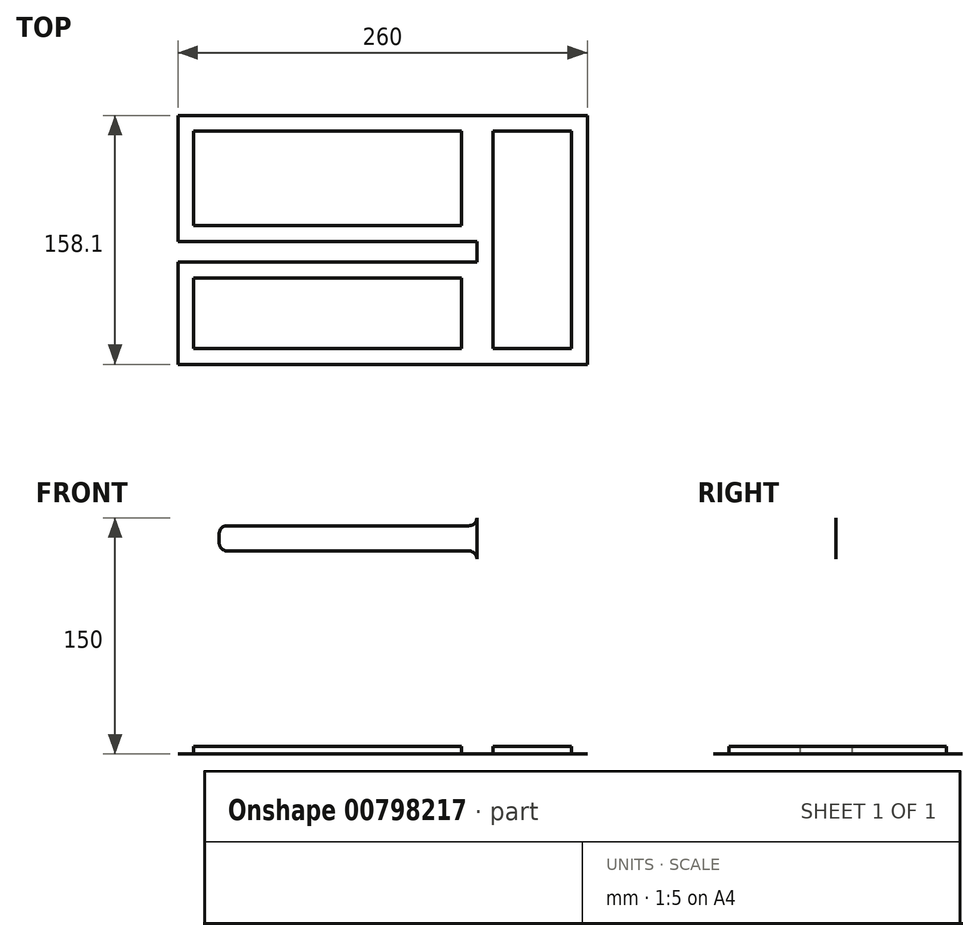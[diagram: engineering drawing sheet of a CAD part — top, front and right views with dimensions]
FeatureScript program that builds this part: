
annotation { "Feature Type Name" : "Feature", "Feature Type Description" : "" }
export const myFeature = defineFeature(function(context is Context, id is Id, definition is map)
    precondition{}
    {
        {
            var Q0;
            Q0=qCreatedBy(makeId("Front.planeOp"),FACE);
            var sketch = newSketch(context, id + "F0", { "sketchPlane" : qUnion([Q0])});
            skLineSegment(sketch, "E0.bottom", {"start": v(100, 120) * mm, "end": v(-100, 120) * mm});
            skLineSegment(sketch, "E0.top", {"start": v(100, -120) * mm, "end": v(-100, -120) * mm});
            skLineSegment(sketch, "E0.left", {"start": v(100, 120) * mm, "end": v(100, -120) * mm});
            skLineSegment(sketch, "E0.right", {"start": v(-100, 120) * mm, "end": v(-100, -120) * mm});
            skPoint(sketch, "E0.middle", {"position": v(0, 0) * mm});
            skSolve(sketch);
        }
        {
            var Q0;
            Q0=makeQuery(id+"F0.imprint","IMPRINT",FACE,{"disambiguationData":[TD([[makeQuery(id+"F0.imprint","IMPRINT",EDGE,{"derivedFrom":sQuery(id+"F0.wireOp",EDGE,"E0.bottom")}),1.0]])]});
            extrude(context, id + "F1", {"entities" : qUnion([Q0]), "depth" : 1 / 50.8 * mm, "offsetDistance" : 25 * mm});
        }
        {
            var Q0;
            Q0=makeQuery(id+"F1.opExtrude","SWEPT_FACE",FACE,{"disambiguationData":[OSD([sQuery(id+"F0.wireOp",EDGE,"E0.left")])]});
            extrude(context, id + "F2", {"entities" : qUnion([Q0]), "operationType" : NewBodyOperationType.ADD, "depth" : 120 * mm, "offsetDistance" : 25 * mm});
        }
        {
            var Q0;
            Q0=makeQuery(id+"F1.opExtrude","CAP_FACE",FACE,{"disambiguationData":[OSD([sQuery(id+"F0.wireOp",EDGE,"E0.bottom"),sQuery(id+"F0.wireOp",EDGE,"E0.top"),sQuery(id+"F0.wireOp",EDGE,"E0.left"),sQuery(id+"F0.wireOp",EDGE,"E0.right")])],"isStart":false});
            var sketch = newSketch(context, id + "F3", { "sketchPlane" : qUnion([Q0])});
            skLineSegment(sketch, "E1.bottom", {"start": v(-100, 120) * mm, "end": v(-13.6, 120) * mm});
            skLineSegment(sketch, "E1.top", {"start": v(-100, -44) * mm, "end": v(-61.8, -44) * mm});
            skLineSegment(sketch, "E1.left", {"start": v(-100, 120) * mm, "end": v(-100, -44) * mm});
            skLineSegment(sketch, "E1.right", {"start": v(-13.6, 120) * mm, "end": v(-13.6, -44) * mm});
            skPoint(sketch, "E2", {"position": v(-56.8, -44) * mm});
            skLineSegment(sketch, "E3", {"start": v(-56.8, -44) * mm, "end": v(-56.8, -58) * mm, "construction": true});
            skLineSegment(sketch, "E4", {"start": v(-61.8, -58) * mm, "end": v(-59.67, -58) * mm});
            skPoint(sketch, "E5", {"position": v(-56.8, -58) * mm});
            skLineSegment(sketch, "E6", {"start": v(-51.8, -58) * mm, "end": v(-51.8, -44) * mm});
            skLineSegment(sketch, "E7", {"start": v(-61.8, -58) * mm, "end": v(-61.8, -44) * mm});
            skLineSegment(sketch, "E8.trimOffspring", {"start": v(-51.8, -44) * mm, "end": v(-13.6, -44) * mm});
            skPoint(sketch, "E9", {"position": v(-56.8, -67.99) * mm});
            skLineSegment(sketch, "E10", {"start": v(-56.8, -58) * mm, "end": v(-56.8, -67.99) * mm, "construction": true});
            skLineSegment(sketch, "E11", {"start": v(-59, -67.98) * mm, "end": v(-59.67, -58) * mm});
            skLineSegment(sketch, "E12", {"start": v(-54.6, -68) * mm, "end": v(-54.6, -58) * mm});
            skLineSegment(sketch, "E13.trimOffspring", {"start": v(-54.6, -58) * mm, "end": v(-51.8, -58) * mm});
            skFitSpline(sketch, "E14", {"points": [v(-56.8, -67.99) * mm, v(-48.64, -88.4) * mm, v(-5.79, -87.52) * mm, v(11.38, -64.83) * mm], "startDerivative": vector(1.52, -51.58) * mm, "endDerivative": vector(22.85, 51.61) * mm, "construction": true});
            skFitSpline(sketch, "E15", {"points": [v(11.38, -64.83) * mm, v(19.18, -38.13) * mm, v(0, -6.57) * mm, v(20.17, 28.85) * mm, v(11.38, 54.12) * mm], "startDerivative": vector(47.45, 107.17) * mm, "endDerivative": vector(-56.95, 91.36) * mm, "construction": true});
            skLineSegment(sketch, "E16", {"start": v(8.93, -70.37) * mm, "end": v(11.38, -64.83) * mm, "construction": true});
            skLineSegment(sketch, "E17", {"start": v(15.02, -56.6) * mm, "end": v(11.38, -64.83) * mm, "construction": true});
            skFitSpline(sketch, "E18.0", {"points": [v(13.4, -65.72) * mm, v(13.86, -64.66) * mm, v(14.94, -62.44) * mm, v(16.76, -58.93) * mm, v(18.6, -55.26) * mm, v(20.25, -51.44) * mm, v(21.5, -47.47) * mm, v(22.03, -44.02) * mm, v(22, -41.2) * mm, v(21.77, -39.42) * mm, v(21.44, -38) * mm, v(21, -36.57) * mm, v(20.3, -34.84) * mm, v(19.24, -32.83) * mm, v(17.58, -30.22) * mm, v(15.18, -27.04) * mm, v(12.04, -23.32) * mm, v(8.92, -19.67) * mm, v(6.1, -16.08) * mm, v(4.23, -13.16) * mm, v(3.15, -10.9) * mm, v(2.57, -9.25) * mm, v(2.3, -7.92) * mm, v(2.2, -6.88) * mm, v(2.2, -5.84) * mm, v(2.35, -4.5) * mm, v(2.8, -2.82) * mm, v(3.48, -1.06) * mm, v(4.69, 1.37) * mm, v(6.69, 4.54) * mm, v(9.62, 8.45) * mm, v(12.8, 12.45) * mm, v(15.98, 16.52) * mm, v(18.4, 19.96) * mm, v(20.05, 22.76) * mm, v(21.12, 24.9) * mm, v(21.84, 26.7) * mm, v(22.28, 28.19) * mm, v(22.62, 29.67) * mm, v(22.87, 31.52) * mm, v(22.9, 34.42) * mm, v(22.35, 37.94) * mm, v(21, 41.92) * mm, v(19.21, 45.66) * mm, v(17.18, 49.15) * mm, v(15.1, 52.39) * mm, v(13.83, 54.35) * mm, v(13.25, 55.28) * mm]});
            skFitSpline(sketch, "E18.1", {"points": [v(-59, -68.05) * mm, v(-58.97, -69.18) * mm, v(-58.8, -71.97) * mm, v(-58.06, -76.25) * mm, v(-56.98, -79.86) * mm, v(-55.87, -82.58) * mm, v(-54.41, -85.25) * mm, v(-52.86, -87.35) * mm, v(-51.4, -88.91) * mm, v(-50.18, -90) * mm, v(-48.84, -91.01) * mm, v(-46.94, -92.2) * mm, v(-44.36, -93.46) * mm, v(-40.97, -94.6) * mm, v(-37.37, -95.4) * mm, v(-32.34, -96.04) * mm, v(-25.75, -96.04) * mm, v(-19.13, -95.04) * mm, v(-14.02, -93.67) * mm, v(-10.34, -92.35) * mm, v(-7.44, -91) * mm, v(-5.24, -89.78) * mm, v(-3.15, -88.46) * mm, v(-0.75, -86.66) * mm, v(2.68, -83.51) * mm, v(6.2, -79.27) * mm, v(9.42, -74.12) * mm, v(11.79, -69.38) * mm, v(12.92, -66.79) * mm, v(13.4, -65.72) * mm]});
            skFitSpline(sketch, "E19.0", {"points": [v(9.37, -63.94) * mm, v(9.89, -62.77) * mm, v(11.03, -60.44) * mm, v(12.86, -56.91) * mm, v(14.62, -53.38) * mm, v(16.13, -49.87) * mm, v(17.21, -46.43) * mm, v(17.62, -43.65) * mm, v(17.6, -41.5) * mm, v(17.43, -40.18) * mm, v(17.18, -39.13) * mm, v(16.87, -38.08) * mm, v(16.32, -36.73) * mm, v(15.43, -35.05) * mm, v(14, -32.76) * mm, v(11.77, -29.82) * mm, v(8.7, -26.2) * mm, v(5.54, -22.49) * mm, v(2.53, -18.68) * mm, v(0.4, -15.37) * mm, v(-0.92, -12.6) * mm, v(-1.68, -10.46) * mm, v(-2.07, -8.6) * mm, v(-2.2, -7.09) * mm, v(-2.2, -5.55) * mm, v(-1.98, -3.65) * mm, v(-1.4, -1.43) * mm, v(-0.54, 0.75) * mm, v(0.88, 3.6) * mm, v(3.09, 7.07) * mm, v(6.15, 11.17) * mm, v(9.37, 15.2) * mm, v(12.46, 19.16) * mm, v(14.72, 22.39) * mm, v(16.2, 24.89) * mm, v(17.1, 26.71) * mm, v(17.8, 28.48) * mm, v(18.25, 30.16) * mm, v(18.47, 31.83) * mm, v(18.5, 34.06) * mm, v(18.07, 36.85) * mm, v(16.94, 40.23) * mm, v(15.34, 43.57) * mm, v(13.44, 46.83) * mm, v(11.42, 49.98) * mm, v(10.12, 51.98) * mm, v(9.51, 52.95) * mm]});
            skFitSpline(sketch, "E19.1", {"points": [v(-54.6, -67.92) * mm, v(-54.57, -68.94) * mm, v(-54.42, -71.46) * mm, v(-53.63, -76.04) * mm, v(-52.28, -79.97) * mm, v(-50.68, -82.89) * mm, v(-49.45, -84.55) * mm, v(-48.31, -85.77) * mm, v(-47.38, -86.6) * mm, v(-46.35, -87.38) * mm, v(-44.84, -88.34) * mm, v(-42.7, -89.37) * mm, v(-38.84, -90.68) * mm, v(-33.31, -91.63) * mm, v(-26.09, -91.64) * mm, v(-20, -90.72) * mm, v(-15.33, -89.46) * mm, v(-12, -88.27) * mm, v(-9.41, -87.07) * mm, v(-7.49, -86) * mm, v(-5.67, -84.85) * mm, v(-3.57, -83.27) * mm, v(-1.3, -81.2) * mm, v(0.72, -78.98) * mm, v(3.1, -75.91) * mm, v(5.57, -71.98) * mm, v(7.8, -67.53) * mm, v(8.89, -65.03) * mm, v(9.37, -63.94) * mm]});
            skLineSegment(sketch, "E20", {"start": v(13.25, 55.28) * mm, "end": v(9.97, 52.23) * mm, "construction": true});
            skLineSegment(sketch, "E21", {"start": v(-59, -68.06) * mm, "end": v(-59, -67.98) * mm});
            skLineSegment(sketch, "E22", {"start": v(-100, 120) * mm, "end": v(220, 120) * mm});
            skLineSegment(sketch, "E23", {"start": v(220, 120) * mm, "end": v(220, -120) * mm});
            skLineSegment(sketch, "E24", {"start": v(220, -120) * mm, "end": v(-100, -120) * mm});
            skLineSegment(sketch, "E25", {"start": v(-100, -120) * mm, "end": v(-100, -44) * mm});
            skLineSegment(sketch, "E26.bottom", {"start": v(220, 120) * mm, "end": v(56.4, 120) * mm});
            skLineSegment(sketch, "E26.top", {"start": v(215, 60) * mm, "end": v(61.4, 60) * mm});
            skLineSegment(sketch, "E26.left", {"start": v(220, 120) * mm, "end": v(220, 65) * mm});
            skLineSegment(sketch, "E26.right", {"start": v(56.4, 120) * mm, "end": v(56.4, 60) * mm, "construction": true});
            skLineSegment(sketch, "E27.bottom", {"start": v(215, 44) * mm, "end": v(61.4, 44) * mm});
            skLineSegment(sketch, "E27.top", {"start": v(220, -120) * mm, "end": v(56.4, -120) * mm});
            skLineSegment(sketch, "E27.left", {"start": v(220, 39) * mm, "end": v(220, -120) * mm});
            skLineSegment(sketch, "E27.right", {"start": v(56.4, 44) * mm, "end": v(56.4, -120) * mm, "construction": true});
            skLineSegment(sketch, "E28", {"start": v(56.4, 55) * mm, "end": v(56.4, 49) * mm});
            skPoint(sketch, "E29.visualSharp", {"position": v(56.4, 60) * mm});
            skArc(sketch, "E29.filletArc", {"start": v(61.4, 60) * mm, "mid": v(57.86, 58.54) * mm, "end": v(56.4, 55) * mm});
            skPoint(sketch, "E30.visualSharp", {"position": v(56.4, 44) * mm});
            skArc(sketch, "E30.filletArc", {"start": v(56.4, 49) * mm, "mid": v(57.86, 45.46) * mm, "end": v(61.4, 44) * mm});
            skPoint(sketch, "E31.visualSharp", {"position": v(220, 60) * mm});
            skArc(sketch, "E31.filletArc", {"start": v(215, 60) * mm, "mid": v(218.54, 61.46) * mm, "end": v(220, 65) * mm});
            skPoint(sketch, "E32.visualSharp", {"position": v(220, 44) * mm});
            skArc(sketch, "E32.filletArc", {"start": v(220, 39) * mm, "mid": v(218.54, 42.54) * mm, "end": v(215, 44) * mm});
            skPoint(sketch, "E33", {"position": v(56.4, 90) * mm});
            skLineSegment(sketch, "E34", {"start": v(56.4, 90) * mm, "end": v(220, 90) * mm, "construction": true});
            skFitSpline(sketch, "E35", {"points": [v(11.38, 54.12) * mm, v(3.8, 74.02) * mm, v(1.8, 120) * mm], "startDerivative": vector(-25.75, 41.3) * mm, "endDerivative": vector(1.23, 85.63) * mm, "construction": true});
            skLineSegment(sketch, "E36", {"start": v(7.9, 59.7) * mm, "end": v(11.38, 54.12) * mm, "construction": true});
            skLineSegment(sketch, "E37", {"start": v(15.67, 47.24) * mm, "end": v(11.38, 54.12) * mm, "construction": true});
            skFitSpline(sketch, "E38.0", {"points": [v(13.25, 55.28) * mm, v(12.21, 56.94) * mm, v(10.32, 60.34) * mm, v(8.39, 65.03) * mm, v(7.1, 69.23) * mm, v(6.28, 72.63) * mm, v(5.6, 76.35) * mm, v(5.05, 80.4) * mm, v(4.62, 84.71) * mm, v(4.2, 90.8) * mm, v(3.92, 98.95) * mm, v(3.88, 109.3) * mm, v(3.96, 116.4) * mm, v(4, 119.97) * mm]});
            skFitSpline(sketch, "E39.0", {"points": [v(9.51, 52.95) * mm, v(8.4, 54.73) * mm, v(6.35, 58.41) * mm, v(4.24, 63.53) * mm, v(2.86, 68.07) * mm, v(1.97, 71.72) * mm, v(1.25, 75.67) * mm, v(0.48, 81.3) * mm, v(-0.14, 88.94) * mm, v(-0.48, 98.88) * mm, v(-0.52, 109.32) * mm, v(-0.44, 116.46) * mm, v(-0.39, 120.03) * mm]});
            skLineSegment(sketch, "E40", {"start": v(9.97, 52.23) * mm, "end": v(9.51, 52.95) * mm});
            skLineSegment(sketch, "E41", {"start": v(-0.39, 120.03) * mm, "end": v(4, 119.97) * mm});
            skPoint(sketch, "E42", {"position": v(86.4, 90) * mm});
            skArc(sketch, "E43", {"start": v(72.32, 87.8) * mm, "mid": v(100.65, 90) * mm, "end": v(72.32, 92.2) * mm});
            skLineSegment(sketch, "E44", {"start": v(56.4, 87.8) * mm, "end": v(72.32, 87.8) * mm});
            skLineSegment(sketch, "E45.MirrorCS", {"start": v(56.4, 92.2) * mm, "end": v(72.32, 92.2) * mm});
            skFitSpline(sketch, "E46", {"points": [v(56.4, 90) * mm, v(34.78, 95.16) * mm, v(30.66, 120) * mm], "startDerivative": vector(-53.5, 1.56) * mm, "endDerivative": vector(1.46, 57.85) * mm, "construction": true});
            skFitSpline(sketch, "E47.0", {"points": [v(56.46, 92.2) * mm, v(54.23, 92.26) * mm, v(50.93, 92.36) * mm, v(46.83, 92.7) * mm, v(43.98, 93.12) * mm, v(41.41, 93.74) * mm, v(39.58, 94.44) * mm, v(38.3, 95.11) * mm, v(37.46, 95.68) * mm, v(36.71, 96.3) * mm, v(36.06, 97) * mm, v(35.47, 97.8) * mm, v(34.77, 99.03) * mm, v(34.04, 100.82) * mm, v(33.41, 103.39) * mm, v(33, 106.28) * mm, v(32.8, 109.45) * mm, v(32.7, 113.95) * mm, v(32.8, 117.53) * mm, v(32.86, 119.94) * mm]});
            skLineSegment(sketch, "E48.0", {"start": v(-95, -115) * mm, "end": v(215, -115) * mm, "construction": true});
            skLineSegment(sketch, "E48.1", {"start": v(-95, 115) * mm, "end": v(-95, -115) * mm, "construction": true});
            skLineSegment(sketch, "E48.2", {"start": v(215, 115) * mm, "end": v(-95, 115) * mm, "construction": true});
            skLineSegment(sketch, "E48.3", {"start": v(215, -115) * mm, "end": v(215, 115) * mm, "construction": true});
            skFitSpline(sketch, "E49.0", {"points": [v(56.34, 87.8) * mm, v(54.1, 87.87) * mm, v(50.73, 87.96) * mm, v(46.35, 88.33) * mm, v(43.18, 88.8) * mm, v(40.16, 89.5) * mm, v(37.8, 90.4) * mm, v(36.06, 91.32) * mm, v(34.82, 92.14) * mm, v(33.68, 93.1) * mm, v(32.65, 94.2) * mm, v(31.77, 95.42) * mm, v(30.77, 97.15) * mm, v(29.83, 99.52) * mm, v(29.08, 102.59) * mm, v(28.63, 105.86) * mm, v(28.4, 109.28) * mm, v(28.3, 114) * mm, v(28.4, 117.64) * mm, v(28.46, 120.06) * mm]});
            skLineSegment(sketch, "E50", {"start": v(56.4, 87.8) * mm, "end": v(56.34, 87.8) * mm});
            skPoint(sketch, "E51", {"position": v(28.46, 120) * mm});
            skLineSegment(sketch, "E52", {"start": v(32.86, 119.94) * mm, "end": v(32.86, 120) * mm});
            skLineSegment(sketch, "E53", {"start": v(28.46, 120) * mm, "end": v(32.86, 120) * mm});
            skLineSegment(sketch, "E54", {"start": v(56.4, -85) * mm, "end": v(220, -85) * mm, "construction": true});
            skSolve(sketch);
        }
        {
            var Q0;
            Q0=makeQuery(id+"F3.imprint","IMPRINT",FACE,{"disambiguationData":[TD([[makeQuery(id+"F3.imprint","IMPRINT",EDGE,{"derivedFrom":sQuery(id+"F3.wireOp",EDGE,"E1.top")}),1.0]])]});
            extrude(context, id + "F4", {"entities" : qUnion([Q0]), "operationType" : NewBodyOperationType.REMOVE, "oppositeDirection" : true, "depth" : 8 * mm, "offsetDistance" : 25 * mm});
        }
        {
            var Q0;
            Q0=makeQuery(id+"F3.imprint","IMPRINT",FACE,{"disambiguationData":[TD([[makeQuery(id+"F3.imprint","IMPRINT",EDGE,{"derivedFrom":sQuery(id+"F3.wireOp",EDGE,"E23")}),-1.0]])]});
            extrude(context, id + "F5", {"entities" : qUnion([Q0]), "operationType" : NewBodyOperationType.REMOVE, "endBound" : BoundingType.UP_TO_NEXT, "oppositeDirection" : true, "depth" : 25 * mm, "offsetDistance" : 25 * mm});
        }
        {
            var Q0;
            {var subQ4=sQuery(id+"F3.wireOp",EDGE,"E43");Q0=makeQuery(id+"F3.imprint","IMPRINT",FACE,{"disambiguationData":[TD([[makeQuery(id+"F3.imprint","IMPRINT",EDGE,{"derivedFrom":subQ4}),1.0]])]});}
            extrude(context, id + "F6", {"entities" : qUnion([Q0]), "operationType" : NewBodyOperationType.REMOVE, "oppositeDirection" : true, "depth" : 6 * mm, "offsetDistance" : 25 * mm});
        }
        {
            var Q0;
            Q0=qCreatedBy(makeId("Top.planeOp"),FACE);
            var Q1;
            Q1=sQuery(id+"F3.wireOp",EDGE,"E54");
            cPlane(context, id + "F7", {"entities" : qUnion([Q0, Q1]), "cplaneType" : CPlaneType.LINE_ANGLE, "offset" : 25 * mm, "angle" : 0 * degree, "width" : 150 * mm, "height" : 150 * mm});
        }
        {
            var Q0;
            Q0=qCreatedBy(id+"F7.planeOp",FACE);
            var sketch = newSketch(context, id + "F8", { "sketchPlane" : qUnion([Q0])});
            skPoint(sketch, "E55.0", {"position": v(13.4, 12.7) * mm});
            skLineSegment(sketch, "E56.0", {"start": v(-100, 12.7) * mm, "end": v(220, 12.7) * mm});
            skLineSegment(sketch, "E57.0", {"start": v(220, 0) * mm, "end": v(-100, 0) * mm});
            skLineSegment(sketch, "E58.0", {"start": v(220, 12.7) * mm, "end": v(220, 0) * mm});
            skLineSegment(sketch, "E59", {"start": v(30.2, 12.7) * mm, "end": v(30.2, 12.9) * mm, "construction": true});
            skLineSegment(sketch, "E60", {"start": v(30.2, 12.9) * mm, "end": v(220.2, 12.9) * mm});
            skLineSegment(sketch, "E61", {"start": v(220.2, 12.9) * mm, "end": v(220.2, -0.2) * mm});
            skLineSegment(sketch, "E62", {"start": v(220.2, -0.2) * mm, "end": v(30.2, -0.2) * mm});
            skLineSegment(sketch, "E63", {"start": v(30.2, -0.2) * mm, "end": v(30.2, -80.2) * mm});
            skLineSegment(sketch, "E64", {"start": v(30.2, -80.2) * mm, "end": v(290.2, -80.2) * mm});
            skLineSegment(sketch, "E65", {"start": v(290.2, -80.2) * mm, "end": v(290.2, 77.9) * mm});
            skLineSegment(sketch, "E66", {"start": v(30.2, 77.9) * mm, "end": v(30.2, 12.9) * mm});
            skLineSegment(sketch, "E67", {"start": v(220.2, 12.9) * mm, "end": v(220.2, 77.9) * mm, "construction": true});
            skLineSegment(sketch, "E68", {"start": v(30.2, 77.9) * mm, "end": v(220.2, 77.9) * mm});
            skLineSegment(sketch, "E69", {"start": v(290.2, 77.9) * mm, "end": v(220.2, 77.9) * mm});
            skLineSegment(sketch, "E70.1", {"start": v(40.2, 67.9) * mm, "end": v(210.2, 67.9) * mm});
            skLineSegment(sketch, "E71", {"start": v(40.2, 67.9) * mm, "end": v(40.2, 22.9) * mm});
            skLineSegment(sketch, "E72", {"start": v(40.2, 22.9) * mm, "end": v(210.2, 22.9) * mm});
            skLineSegment(sketch, "E73", {"start": v(210.2, 22.9) * mm, "end": v(210.2, 67.9) * mm});
            skLineSegment(sketch, "E74", {"start": v(220.2, -0.2) * mm, "end": v(220.2, -80.2) * mm, "construction": true});
            skLineSegment(sketch, "E75", {"start": v(40.2, -10.2) * mm, "end": v(40.2, -70.2) * mm});
            skLineSegment(sketch, "E76", {"start": v(210.2, -10.2) * mm, "end": v(210.2, -70.2) * mm});
            skLineSegment(sketch, "E77", {"start": v(210.2, -70.2) * mm, "end": v(40.2, -70.2) * mm});
            skLineSegment(sketch, "E78", {"start": v(40.2, -10.2) * mm, "end": v(210.2, -10.2) * mm});
            skLineSegment(sketch, "E79.bottom", {"start": v(230.2, -70.2) * mm, "end": v(280.2, -70.2) * mm});
            skLineSegment(sketch, "E79.top", {"start": v(230.2, 67.9) * mm, "end": v(280.2, 67.9) * mm});
            skLineSegment(sketch, "E79.left", {"start": v(230.2, -70.2) * mm, "end": v(230.2, 67.9) * mm});
            skLineSegment(sketch, "E79.right", {"start": v(280.2, -70.2) * mm, "end": v(280.2, 67.9) * mm});
            skSolve(sketch);
        }
        {
            var Q0;
            Q0=makeQuery(id+"F8.imprint","IMPRINT",FACE,{"disambiguationData":[TD([[makeQuery(id+"F8.imprint","IMPRINT",EDGE,{"derivedFrom":sQuery(id+"F8.wireOp",EDGE,"E60")}),1.0]])]});
            extrude(context, id + "F9", {"entities" : qUnion([Q0]), "oppositeDirection" : true, "depth" : 1 / 50.8 * mm, "offsetDistance" : 25 * mm});
        }
        {
            var Q0;
            Q0=makeQuery(id+"F8.imprint","IMPRINT",FACE,{"disambiguationData":[TD([[makeQuery(id+"F8.imprint","IMPRINT",EDGE,{"derivedFrom":sQuery(id+"F8.wireOp",EDGE,"E70.1")}),-1.0]])]});
            var Q1;
            Q1=makeQuery(id+"F8.imprint","IMPRINT",FACE,{"disambiguationData":[TD([[makeQuery(id+"F8.imprint","IMPRINT",EDGE,{"derivedFrom":sQuery(id+"F8.wireOp",EDGE,"E79.bottom")}),1.0]])]});
            var Q2;
            Q2=makeQuery(id+"F8.imprint","IMPRINT",FACE,{"disambiguationData":[TD([[makeQuery(id+"F8.imprint","IMPRINT",EDGE,{"derivedFrom":sQuery(id+"F8.wireOp",EDGE,"E75")}),1.0]])]});
            extrude(context, id + "F10", {"entities" : qUnion([Q0, Q1, Q2]), "operationType" : NewBodyOperationType.ADD, "oppositeDirection" : true, "depth" : 5 * mm, "offsetDistance" : 25 * mm});
        }
    });
